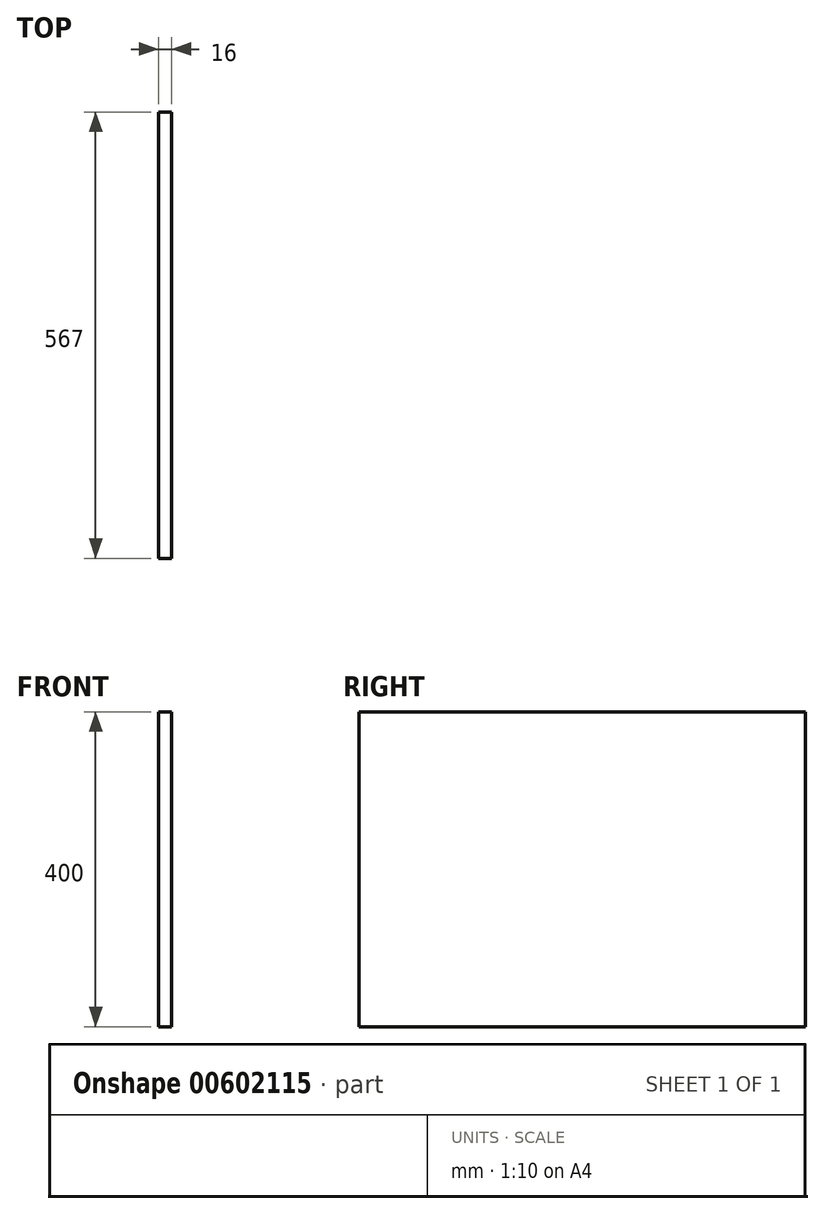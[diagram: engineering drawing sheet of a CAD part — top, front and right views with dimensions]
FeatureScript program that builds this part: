
annotation { "Feature Type Name" : "Feature", "Feature Type Description" : "" }
export const myFeature = defineFeature(function(context is Context, id is Id, definition is map)
    precondition{}
    {
        {
            var Q0;
            Q0=qCreatedBy(makeId("Right.planeOp"),FACE);
            var sketch = newSketch(context, id + "F0", { "sketchPlane" : qUnion([Q0])});
            skLineSegment(sketch, "E0.bottom", {"start": v(0, 0) * mm, "end": v(-567, 0) * mm});
            skLineSegment(sketch, "E0.top", {"start": v(0, 400) * mm, "end": v(-567, 400) * mm});
            skLineSegment(sketch, "E0.left", {"start": v(0, 0) * mm, "end": v(0, 400) * mm});
            skLineSegment(sketch, "E0.right", {"start": v(-567, 0) * mm, "end": v(-567, 400) * mm});
            skSolve(sketch);
        }
        {
            var Q0;
            Q0 = qSketchRegion(id + "F0", true);
            extrude(context, id + "F1", {"entities" : qUnion([Q0]), "depth" : 16 * mm, "offsetDistance" : 25 * mm});
        }
    });
